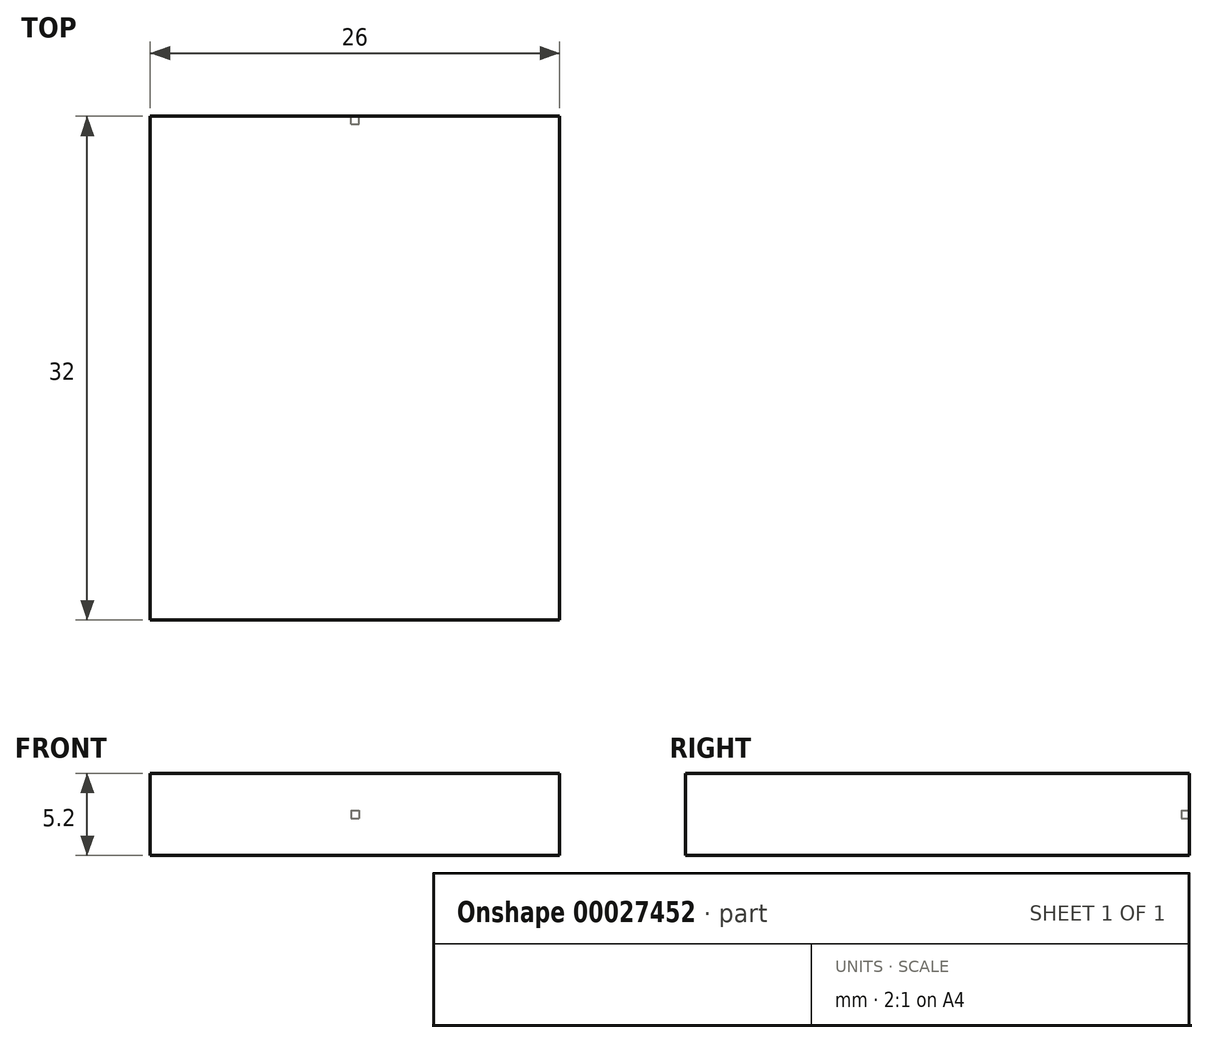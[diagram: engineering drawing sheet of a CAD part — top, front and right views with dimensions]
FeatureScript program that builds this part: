
annotation { "Feature Type Name" : "Feature", "Feature Type Description" : "" }
export const myFeature = defineFeature(function(context is Context, id is Id, definition is map)
    precondition{}
    {
        {
            var Q0;
            Q0=qCreatedBy(makeId("Top.planeOp"),FACE);
            var sketch = newSketch(context, id + "F0", { "sketchPlane" : qUnion([Q0])});
            skLineSegment(sketch, "E0.rect.bottom", {"start": v(13, 16) * mm, "end": v(-13, 16) * mm});
            skLineSegment(sketch, "E0.rect.top", {"start": v(13, -16) * mm, "end": v(-13, -16) * mm});
            skLineSegment(sketch, "E0.rect.left", {"start": v(13, 16) * mm, "end": v(13, -16) * mm});
            skLineSegment(sketch, "E0.rect.right", {"start": v(-13, 16) * mm, "end": v(-13, -16) * mm});
            skPoint(sketch, "E0.rect.middle", {"position": v(0, 0) * mm});
            skSolve(sketch);
        }
        {
            var Q0;
            Q0 = qSketchRegion(id + "F0", true);
            extrude(context, id + "F1", {"entities" : qUnion([Q0]), "depth" : 5.2 * mm});
        }
        {
            var Q0;
            Q0=makeQuery(id+"F1.opExtrude","SWEPT_FACE",FACE,{"disambiguationData":[OSD([sQuery(id+"F0.wireOp",EDGE,"E0.rect.bottom")])]});
            var sketch = newSketch(context, id + "F2", { "sketchPlane" : qUnion([Q0])});
            skLineSegment(sketch, "E1", {"start": v(0, 0) * mm, "end": v(0, 5.2) * mm, "construction": true});
            skLineSegment(sketch, "E2.rect.bottom", {"start": v(0.25, 2.85) * mm, "end": v(-0.25, 2.85) * mm});
            skLineSegment(sketch, "E2.rect.top", {"start": v(0.25, 2.35) * mm, "end": v(-0.25, 2.35) * mm});
            skLineSegment(sketch, "E2.rect.left", {"start": v(0.25, 2.85) * mm, "end": v(0.25, 2.35) * mm});
            skLineSegment(sketch, "E2.rect.right", {"start": v(-0.25, 2.85) * mm, "end": v(-0.25, 2.35) * mm});
            skPoint(sketch, "E2.rect.middle", {"position": v(0, 2.6) * mm});
            skSolve(sketch);
        }
        {
            var Q0;
            Q0 = qSketchRegion(id + "F2", true);
            extrude(context, id + "F3", {"entities" : qUnion([Q0]), "operationType" : NewBodyOperationType.REMOVE, "oppositeDirection" : true, "depth" : 0.5 * mm});
        }
    });
